# Revit family: IS_Conca_T3988_BIM_IT
name_source: partatom
category: Plumbing Fixtures
revit_build: Autodesk Revit 2017 (Build: 20160225_1515(x64)
units: mm (PartAtom-declared; Revit-internal decimal feet)

## family parameters
Always vertical = No
Cut with Voids When Loaded = No
OmniClass Number = 23.45.05.14.21.11
OmniClass Title = Bath/Shower Units
Part Type = Normal
Room Calculation Point = No
Round Connector Dimension = Use Diameter
Shared = No
Work Plane-Based = No

## types (6) — shared parameters
Accessori = https://www.idealstandard.it
Aiuto = https://www.idealstandard.it
AltezzaNominale = 372 mm
Autore = Ideal Standard
BIMobject category = Storage
BIMobject category code = sanitary-storage
BIMobject main category = Sanitary
BIMobject main category code = sanitary
Brand = https://www.idealstandard.it
DescrizioneClassifcazioneUni2015 = Bathroom cabinets
DurataGaranzia = 2
DurataGaranziaProdotti = 2
Forma = Rettangolare
Garanzia = Garanzia Idealstandard
IfcEsportaCome = IfcFurnitureType
InformaziniGaranzia = https://www.idealstandard.it
InformazioniDiProdotto = http://www.idealstandard.it
InformazioniGaranzia = https://www.idealstandard.it
Installation instructions = https://www.idealspec.co.uk
InstruzioniInstallazione = https://www.idealstandard.it
LarghezzaNominale = 1000 mm  [stored 3.28084 ft]
Maniglia = No
Manufacturer = Ideal Standard
Materiale = Ceramics
NominalDepth = 505 mm  [stored 1.65682 ft]
NominalHeight = 359 mm
NominalWidth = 1000 mm  [stored 3.28084 ft]
PesoNetto = 34.7
PiattoDoccia = No
Product group = Bathroom_Furniture
Produttore = Ideal Standard
ProfonditaNominale = 505 mm  [stored 1.65682 ft]
Revisione = 1
RiferimentoClassificazioneUni2015 = Pr_40_30_78_03
Spazio = Interno
Telefono = 800 652 290
TipoEspotazioneIfc = Bathroom cabinets
URL = https://www.ideal-standard.co.uk
Uniclass 2015 Code = Pr_40_30_78_03
Uniclass 2015 Name = Bathroom cabinets
UnitàDurata = Anno
UnitàDurataGaranzia = Anno
UnitàLineare = Milimitre
UnitàMonetaria = €
UnitàSuperficie = Milimitre
UnitàVolume = Litri
Versione = 1
VersioneClassificazioneUni2015 = v1.1
zero-valued in all types: CostoDiSostituzione, DimensioneScarico, LunghezzaNominale, Nominal depth, Nominal height, SeatMaterial, SpessoreDelMateriale, SpilloverLivello, Weight Net (Kg)

## per-type parameters (varying)
| type | Caratteristiche | CodiceABarre | CodiceArticolo | Colore | Description | Desrizione | Finitura | Model | ModelloDiRiferimento | Nome | NomeOggettoBim | NumeroDiModello |
| T3988Y1 - Conca BSN UN 100X50X37 1 DR NOWTOP WHMT - T3988 - Y1_MattWhite | Mobile sottolavabo, 1000 x 505 x 370mm, 1 cassetto esterno senza piano da appoggio. Dotato di tecnologia push open e soft close. Cassetti in metallo.. Finitura Antracite laccato opaco. | 8014140462439 | T3988Y1 | Matt anthracite | Vanity unit, 1000 x 505 x 370mm, 1 external drawer without countertop. Equipped with push open and soft close technology. Matt lacquered Anthracite finish. | Mobile sottolavabo, 1000 x 505 x 370mm, 1 cassetto esterno senza piano da appoggio. Dotato di tecnologia push open e soft close. Cassetti in metallo.. Finitura Antracite laccato opaco. | Matt anthracite | T3988Y1 | T3988Y1 | BathroomCabinets_Conca_T3988Y1_IdealStandard | ISI_IdealStandard_Bathroom Cabinets_Conca_T3988Y1 | T3988Y1 |
| T3988Y2 - Conca BSN UN 100X50X37 1 DR NOWTOP WHMT - T3988 - Y2_MattAntracite | Mobile sottolavabo, 1000 x 505 x 370mm, 1 cassetto esterno senza piano da appoggio. Dotato di tecnologia push open e soft close. Cassetti in metallo.. Finitura Sunset laccato opaco. | 8014140462446 | T3988Y2 | Matt Sunset | Vanity unit, 1000 x 505 x 370mm, 1 external drawer without countertop. Equipped with push open and soft close technology. Sunset matt lacquer finish. | Mobile sottolavabo, 1000 x 505 x 370mm, 1 cassetto esterno senza piano da appoggio. Dotato di tecnologia push open e soft close. Cassetti in metallo.. Finitura Sunset laccato opaco. | Matt Sunset | T3988Y2 | T3988Y2 | BathroomCabinets_Conca_T3988Y2_IdealStandard | ISI_IdealStandard_Bathroom Cabinets_Conca_T3988Y2 | T3988Y2 |
| T3988Y3 - Conca BSN UN 100X50X37 1 DR NOWTOP WHMT - T3988 - Y3_MattSunset | Mobile sottolavabo, 1000 x 505 x 370mm, 1 cassetto esterno senza piano da appoggio. Dotato di tecnologia push open e soft close. Cassetti in metallo.. Finitura Rovere affumicato scuro. | 8014140462453 | T3988Y3 | Matt Sunset | Vanity unit, 1000 x 505 x 370mm, 1 external drawer without countertop. Equipped with push open and soft close technology. Dark smoked oak finish. | Mobile sottolavabo, 1000 x 505 x 370mm, 1 cassetto esterno senza piano da appoggio. Dotato di tecnologia push open e soft close. Cassetti in metallo.. Finitura Rovere affumicato scuro. | Matt Sunset | T3988Y3 | T3988Y3 | BathroomCabinets_Conca_T3988Y3_IdealStandard | ISI_IdealStandard_Bathroom Cabinets_Conca_T3988Y3 | T3988Y3 |
| T3988Y4 - Conca BSN UN 100X50X37 1 DR NOWTOP WHMT - T3988 - Y4_SmokedOak | Mobile sottolavabo, 1000 x 505 x 370mm, 1 cassetto esterno senza piano da appoggio. Dotato di tecnologia push open e soft close. Cassetti in metallo.. Finitura Noce scuro. | 8014140462460 | T3988Y4 | Dark Walnut | Vanity unit, 1000 x 505 x 370mm, 1 external drawer without countertop. Equipped with push open and soft close technology. Dark Walnut finish. | Mobile sottolavabo, 1000 x 505 x 370mm, 1 cassetto esterno senza piano da appoggio. Dotato di tecnologia push open e soft close. Cassetti in metallo.. Finitura Noce scuro. | Dark Walnut | T3988Y4 | T3988Y4 | BathroomCabinets_Conca_T3988Y4_IdealStandard | ISI_IdealStandard_Bathroom Cabinets_Conca_T3988Y4 | T3988Y4 |
| T3988Y5 - Conca BSN UN 100X50X37 1 DR NOWTOP WHMT - T3988 - Y5_DarkWalnut | Mobile sottolavabo, 1000 x 505 x 370mm, 1 cassetto esterno senza piano da appoggio. Dotato di tecnologia push open e soft close. Cassetti in metallo.. Finitura Legno chiaro. | 8014140462477 | T3988Y5 | Dark Walnut | Vanity unit, 1000 x 505 x 370mm, 1 external drawer without countertop. Equipped with push open and soft close technology. Dark Walnut finish | Mobile sottolavabo, 1000 x 505 x 370mm, 1 cassetto esterno senza piano da appoggio. Dotato di tecnologia push open e soft close. Cassetti in metallo.. Finitura Legno chiaro. | Dark Walnut | T3988Y5 | T3988Y5 | BathroomCabinets_Conca_T3988Y5_IdealStandard | ISI_IdealStandard_Bathroom Cabinets_Conca_T3988Y5 | T3988Y5 |
| T3988Y6 - Conca BSN UN 100X50X37 1 DR NOWTOP WHMT - T3988 - Y6_LightOak | Mobile sottolavabo, 1000 x 505 x 370mm, 1 cassetto esterno senza piano da appoggio. Dotato di tecnologia push open e soft close. Cassetti in metallo. | 8014140462484 | T3988Y6 | Light Oak | Vanity unit, 1000 x 505 x 370mm, 1 external drawer without countertop. Equipped with push open and soft close technology. | Mobile sottolavabo, 1000 x 505 x 370mm, 1 cassetto esterno senza piano da appoggio. Dotato di tecnologia push open e soft close. Cassetti in metallo. | Light Oak | T3988Y6 | T3988Y6 | BathroomCabinets_Conca_T3988Y6_IdealStandard | ISI_IdealStandard_Bathroom Cabinets_Conca_T3988Y6 | T3988Y6 |

note: [stored X ft] marks values corroborated as IEEE doubles in the binary element streams (Revit-internal decimal feet)

## geometry (parser evidence)
native form markers: Sweep x3
no freeform markers — native parametric forms only
